# Revit family: РИДАН_Клапан регулирующий VRB-2R
name_source: partatom
category: Арматура трубопроводов
units: mm (PartAtom-declared; Revit-internal decimal feet)

## family parameters
Всегда вертикально = Да
На основе рабочей плоскости = Нет
Общий = Нет
При загрузке вырезать с полостями = Нет
Размер круглого соединителя = Использовать диаметр
Тип детали = Вставляется

## types (10) — shared parameters
ADSK_Версия Revit = 2019
ADSK_Версия семейства = 1.0
ADSK_Единица измерения = шт.
ADSK_Завод-изготовитель = ООО «Ридан-Трейд»
ADSK_Количество = 1
ADSK_Количество фаз = 1
ADSK_Коэффициент мощности = 1
ADSK_Потеря давления жидкости = 0.0 Па
ADSK_Расход жидкости = 0.000 м³/ч
LT = VRB-2R
URL = https://ridan.ru

## per-type parameters (varying)
| type | ADSK_Диаметр условный | ADSK_Классификация нагрузок | ADSK_Код изделия | ADSK_Марка | ADSK_Масса | ADSK_Наименование | ADSK_Номинальная мощность | ADSK_Полная мощность | ADSK_Пропускная способность | a | b | c | d | e | f | g | h | i | j | k | Тип |
| DN15 Kvs=0,63 | 15 мм | Прочее | 065Z0231R | VRB-2R DN15 | 1.25 | Клапан регулирующий VRB-2R с внутренней резьбой PN25, Tmax=130C, DN15, Kvs=0,63 м3\ч | 7 Вт | 7 В·А | 0.630 м³/ч | 15 мм | 55 мм | 28 мм | 44 мм | 38 мм | 63 мм | 22 мм | 33 мм | 25 мм | 34 мм | 21 мм | 1 |
| DN15 Kvs=1 | 15 мм |  | 065Z0232R | VRB-2R DN15 | 1.25 | Клапан регулирующий VRB-2R с внутренней резьбой PN25, Tmax=130C, DN15, Kvs=1 м3\ч | 0 Вт | 0 В·А | 0.630 м³/ч | 15 мм | 55 мм | 28 мм | 44 мм | 38 мм | 63 мм | 22 мм | 33 мм | 25 мм | 34 мм | 21 мм | 2 |
| DN15 Kvs=1,6 | 15 мм |  | 065Z0233R | VRB-2R DN15 | 1.25 | Клапан регулирующий VRB-2R с внутренней резьбой PN25, Tmax=130C, DN15, Kvs=1,6 м3\ч | 0 Вт | 0 В·А | 0.630 м³/ч | 15 мм | 55 мм | 28 мм | 44 мм | 38 мм | 63 мм | 22 мм | 33 мм | 25 мм | 34 мм | 21 мм | 3 |
| DN15 Kvs=2,5 | 15 мм |  | 065Z0234R | VRB-2R DN15 | 1.25 | Клапан регулирующий VRB-2R с внутренней резьбой PN25, Tmax=130C, DN15, Kvs=2,5 м3\ч | 0 Вт | 0 В·А | 0.630 м³/ч | 15 мм | 55 мм | 28 мм | 44 мм | 38 мм | 63 мм | 22 мм | 33 мм | 25 мм | 34 мм | 21 мм | 4 |
| DN15 Kvs=4 | 15 мм |  | 065Z0235R | VRB-2R DN15 | 1.25 | Клапан регулирующий VRB-2R с внутренней резьбой PN25, Tmax=130C, DN15, Kvs=4 м3\ч | 0 Вт | 0 В·А | 0.630 м³/ч | 15 мм | 55 мм | 28 мм | 44 мм | 38 мм | 63 мм | 22 мм | 33 мм | 25 мм | 34 мм | 21 мм | 5 |
| DN20 Kvs=6,3 | 20 мм |  | 065Z0236R | VRB-2R DN20 | 1.25 | Клапан регулирующий VRB-2R с внутренней резьбой PN25, Tmax=130C, DN20 | 0 Вт | 0 В·А | 6.300 м³/ч | 15 мм | 55 мм | 28 мм | 44 мм | 38 мм | 63 мм | 22 мм | 33 мм | 25 мм | 34 мм | 26 мм | 6 |
| DN25 Kvs=8 | 25 мм |  | 065Z0237R | VRB-2R DN25 | 1.4 | Клапан регулирующий VRB-2R с внутренней резьбой PN25, Tmax=130C, DN25 | 0 Вт | 0 В·А | 8.000 м³/ч | 21 мм | 49 мм | 25 мм | 46 мм | 41 мм | 61 мм | 22 мм | 40 мм | 26 мм | 41 мм | 34 мм | 6 |
| DN32 Kvs=12 | 32 мм |  | 065Z0238R | VRB-2R DN32 | 2.15 | Клапан регулирующий VRB-2R с внутренней резьбой PN25, Tmax=130C, DN32 | 0 Вт | 0 В·А | 12.000 м³/ч | 19 мм | 67 мм | 34 мм | 46 мм | 50 мм | 69 мм | 26 мм | 49 мм | 30 мм | 50 мм | 42 мм | 6 |
| DN40 Kvs=20 | 40 мм |  | 065Z0239R | VRB-2R DN40 | 2.5 | Клапан регулирующий VRB-2R с внутренней резьбой PN25, Tmax=130C, DN40 | 0 Вт | 0 В·А | 20.000 м³/ч | 19 мм | 82 мм | 41 мм | 46 мм | 64 мм | 79 мм | 30 мм | 56 мм | 38 мм | 58 мм | 48 мм | 6 |
| DN50 Kvs=30 | 50 мм |  | 065Z0240R | VRB-2R DN50 | 2.5 | Клапан регулирующий VRB-2R с внутренней резьбой PN25, Tmax=130C, DN50 | 0 Вт | 0 В·А | 30.000 м³/ч | 19 мм | 102 мм | 51 мм | 46 мм | 69 мм | 93 мм | 38 мм | 68 мм | 48 мм | 69 мм | 60 мм | 6 |
